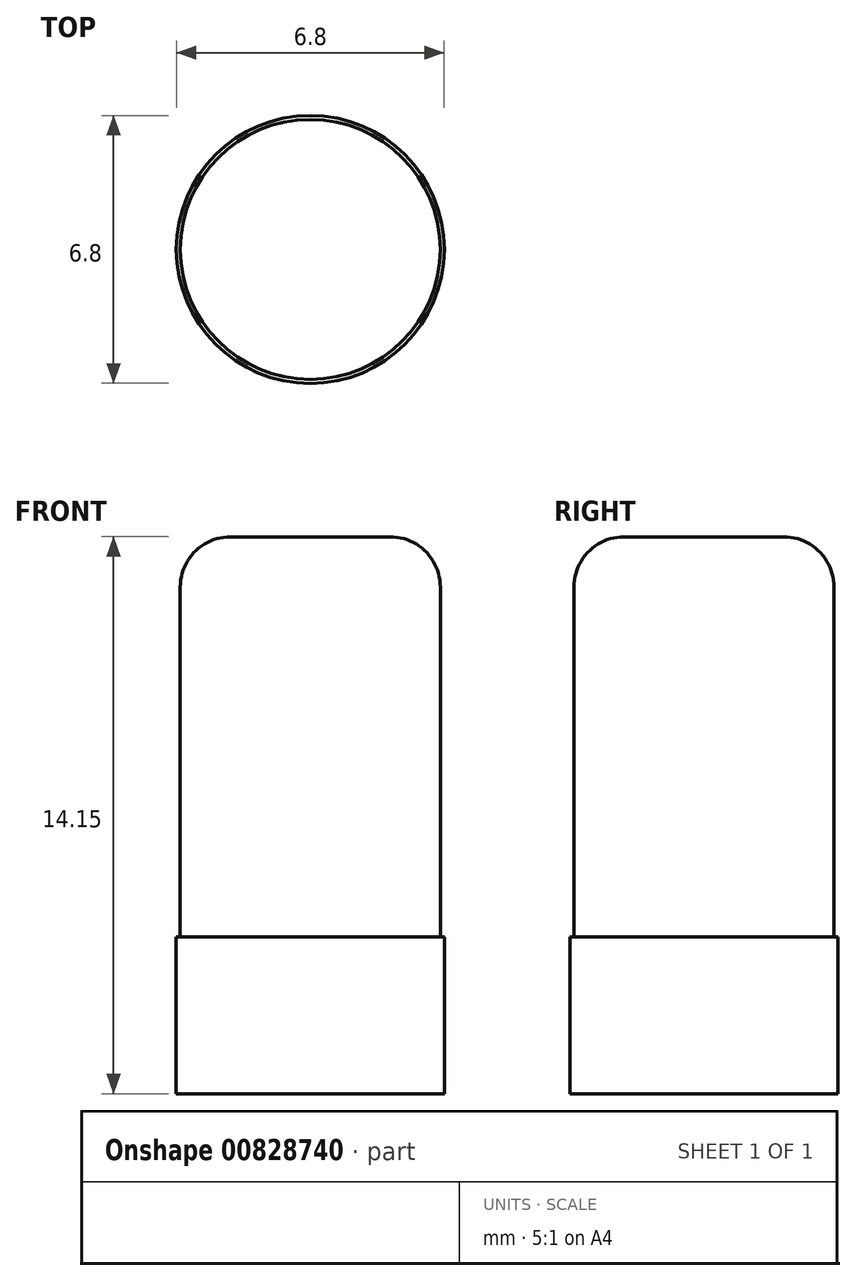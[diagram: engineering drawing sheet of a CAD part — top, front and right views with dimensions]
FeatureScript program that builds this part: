
annotation { "Feature Type Name" : "Feature", "Feature Type Description" : "" }
export const myFeature = defineFeature(function(context is Context, id is Id, definition is map)
    precondition{}
    {
        {
            var Q0;
            Q0=qCreatedBy(makeId("Top.planeOp"),FACE);
            var sketch = newSketch(context, id + "F0", { "sketchPlane" : qUnion([Q0])});
            skCircle(sketch, "E0", {"center": v(0, 0) * mm, "radius": 3.4 * mm});
            skSolve(sketch);
        }
        {
            var Q0;
            Q0=makeQuery(id+"F0.imprint","IMPRINT",FACE,{"disambiguationData":[TD([[makeQuery(id+"F0.imprint","IMPRINT",EDGE,{"derivedFrom":sQuery(id+"F0.wireOp",EDGE,"E0")}),1.0]])]});
            extrude(context, id + "F1", {"entities" : qUnion([Q0]), "depth" : 4 * mm, "offsetDistance" : 25.4 * mm});
        }
        {
            var Q0;
            Q0=makeQuery(id+"F1.opExtrude","CAP_FACE",FACE,{"disambiguationData":[OSD([sQuery(id+"F0.wireOp",EDGE,"E0")])],"isStart":false});
            var sketch = newSketch(context, id + "F2", { "sketchPlane" : qUnion([Q0])});
            skCircle(sketch, "E1", {"center": v(0, 0) * mm, "radius": 3.3 * mm});
            skSolve(sketch);
        }
        {
            var Q0;
            Q0=makeQuery(id+"F2.imprint","IMPRINT",FACE,{"disambiguationData":[TD([[makeQuery(id+"F2.imprint","IMPRINT",EDGE,{"derivedFrom":sQuery(id+"F2.wireOp",EDGE,"E1")}),1.0]])]});
            extrude(context, id + "F3", {"entities" : qUnion([Q0]), "operationType" : NewBodyOperationType.ADD, "depth" : 10.16 * mm, "offsetDistance" : 25.4 * mm});
        }
        {
            var Q0;
            Q0=makeQuery(id+"F3.opExtrude","CAP_EDGE",EDGE,{"disambiguationData":[OSD([sQuery(id+"F2.wireOp",EDGE,"E1")])],"isStart":true});
            var Q1;
            Q1=makeQuery(id+"F3.opExtrude","CAP_EDGE",EDGE,{"disambiguationData":[OSD([sQuery(id+"F2.wireOp",EDGE,"E1")])],"isStart":false});
            fillet(context, id + "F4", {"entities" : qUnion([Q0, Q1]), "radius" : 1.27 * mm, "tangentPropagation" : true, "allowEdgeOverflow" : false});
        }
    });
